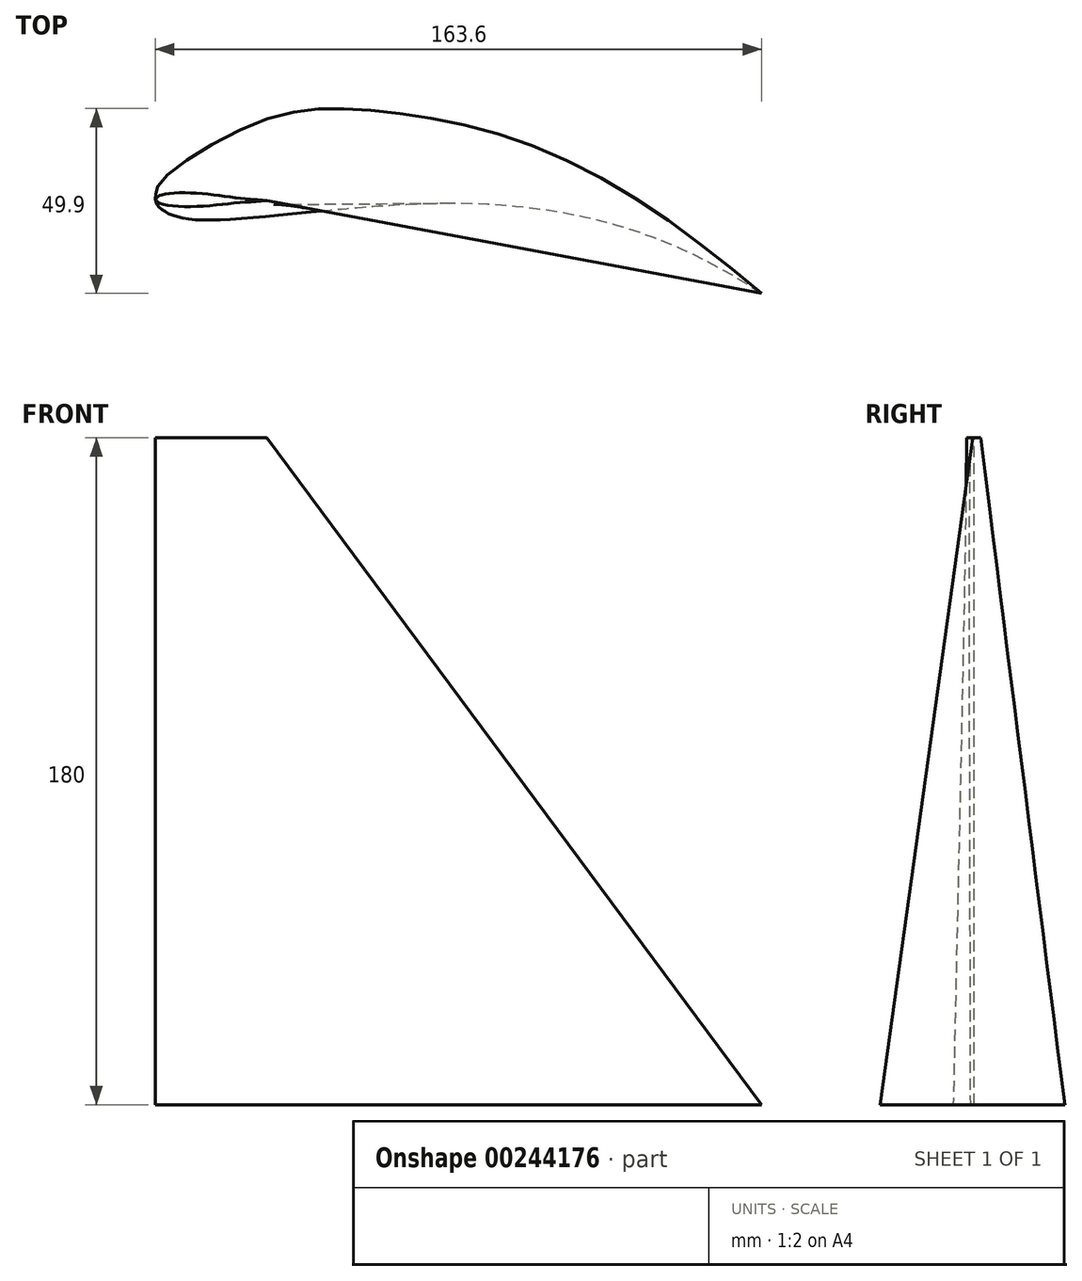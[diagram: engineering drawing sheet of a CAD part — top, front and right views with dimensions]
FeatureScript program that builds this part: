
annotation { "Feature Type Name" : "Feature", "Feature Type Description" : "" }
export const myFeature = defineFeature(function(context is Context, id is Id, definition is map)
    precondition{}
    {
        {
            var Q0;
            Q0=qCreatedBy(makeId("Top.planeOp"),FACE);
            var sketch = newSketch(context, id + "F0", { "sketchPlane" : qUnion([Q0])});
            skLineSegment(sketch, "E0", {"start": v(1.56, 5.68) * mm, "end": v(5.56, 9.57) * mm});
            skLineSegment(sketch, "E1", {"start": v(5.56, 9.57) * mm, "end": v(7.64, 11.4) * mm});
            skLineSegment(sketch, "E2", {"start": v(7.64, 11.4) * mm, "end": v(10.4, 13.54) * mm});
            skLineSegment(sketch, "E3", {"start": v(10.4, 13.54) * mm, "end": v(12.1, 14.65) * mm});
            skLineSegment(sketch, "E4", {"start": v(12.1, 14.65) * mm, "end": v(14.51, 16.01) * mm});
            skLineSegment(sketch, "E5", {"start": v(14.51, 16.01) * mm, "end": v(17.02, 17.22) * mm});
            skLineSegment(sketch, "E6", {"start": v(17.02, 17.22) * mm, "end": v(19.6, 18.28) * mm});
            skLineSegment(sketch, "E7", {"start": v(19.6, 18.28) * mm, "end": v(22.25, 19.22) * mm});
            skLineSegment(sketch, "E8", {"start": v(22.25, 19.22) * mm, "end": v(25.63, 20.25) * mm});
            skLineSegment(sketch, "E9", {"start": v(25.63, 20.25) * mm, "end": v(27.63, 20.8) * mm});
            skLineSegment(sketch, "E10", {"start": v(27.63, 20.8) * mm, "end": v(30.34, 21.45) * mm});
            skLineSegment(sketch, "E11", {"start": v(30.34, 21.45) * mm, "end": v(33.06, 22.02) * mm});
            skLineSegment(sketch, "E12", {"start": v(33.06, 22.02) * mm, "end": v(35.8, 22.52) * mm});
            skLineSegment(sketch, "E13", {"start": v(35.8, 22.52) * mm, "end": v(38.53, 22.94) * mm});
            skLineSegment(sketch, "E14", {"start": v(38.53, 22.94) * mm, "end": v(41.28, 23.3) * mm});
            skLineSegment(sketch, "E15", {"start": v(41.28, 23.3) * mm, "end": v(45.44, 23.69) * mm});
            skLineSegment(sketch, "E16", {"start": v(45.44, 23.69) * mm, "end": v(52.36, 24.01) * mm});
            skLineSegment(sketch, "E17", {"start": v(52.36, 24.01) * mm, "end": v(57.92, 23.98) * mm});
            skLineSegment(sketch, "E18", {"start": v(57.92, 23.98) * mm, "end": v(63.48, 23.67) * mm});
            skLineSegment(sketch, "E19", {"start": v(63.48, 23.67) * mm, "end": v(68.2, 23.2) * mm});
            skLineSegment(sketch, "E20", {"start": v(68.2, 23.2) * mm, "end": v(74.5, 22.25) * mm});
            skLineSegment(sketch, "E21", {"start": v(74.5, 22.25) * mm, "end": v(79.94, 21.16) * mm});
            skLineSegment(sketch, "E22", {"start": v(79.94, 21.16) * mm, "end": v(85.34, 19.84) * mm});
            skLineSegment(sketch, "E23", {"start": v(85.34, 19.84) * mm, "end": v(91.78, 17.96) * mm});
            skLineSegment(sketch, "E24", {"start": v(91.78, 17.96) * mm, "end": v(95.97, 16.57) * mm});
            skLineSegment(sketch, "E25", {"start": v(95.97, 16.57) * mm, "end": v(101.2, 14.66) * mm});
            skLineSegment(sketch, "E26", {"start": v(101.2, 14.66) * mm, "end": v(106.35, 12.57) * mm});
            skLineSegment(sketch, "E27", {"start": v(106.35, 12.57) * mm, "end": v(111.41, 10.3) * mm});
            skLineSegment(sketch, "E28", {"start": v(111.41, 10.3) * mm, "end": v(114.54, 8.79) * mm});
            skLineSegment(sketch, "E29", {"start": v(114.54, 8.79) * mm, "end": v(121.24, 5.25) * mm});
            skLineSegment(sketch, "E30", {"start": v(121.24, 5.25) * mm, "end": v(126.03, 2.48) * mm});
            skLineSegment(sketch, "E31", {"start": v(126.03, 2.48) * mm, "end": v(130.76, -0.45) * mm});
            skLineSegment(sketch, "E32", {"start": v(130.76, -0.45) * mm, "end": v(134.68, -3) * mm});
            skLineSegment(sketch, "E33", {"start": v(134.68, -3) * mm, "end": v(140.13, -6.74) * mm});
            skLineSegment(sketch, "E34", {"start": v(140.13, -6.74) * mm, "end": v(144.69, -10.02) * mm});
            skLineSegment(sketch, "E35", {"start": v(144.69, -10.02) * mm, "end": v(150.73, -14.63) * mm});
            skLineSegment(sketch, "E36", {"start": v(150.73, -14.63) * mm, "end": v(153.15, -16.57) * mm});
            skLineSegment(sketch, "E37", {"start": v(153.15, -16.57) * mm, "end": v(155.17, -18.23) * mm});
            skLineSegment(sketch, "E38", {"start": v(155.17, -18.23) * mm, "end": v(157.28, -19.98) * mm});
            skLineSegment(sketch, "E39", {"start": v(157.28, -19.98) * mm, "end": v(159.53, -21.87) * mm});
            skLineSegment(sketch, "E40", {"start": v(159.53, -21.87) * mm, "end": v(161.04, -23.14) * mm});
            skLineSegment(sketch, "E41", {"start": v(161.04, -23.14) * mm, "end": v(162.55, -24.41) * mm});
            skLineSegment(sketch, "E42", {"start": v(162.55, -24.41) * mm, "end": v(163.03, -24.83) * mm});
            skLineSegment(sketch, "E43", {"start": v(163.03, -24.83) * mm, "end": v(163.34, -25.1) * mm});
            skLineSegment(sketch, "E44", {"start": v(163.34, -25.1) * mm, "end": v(163.57, -25.34) * mm});
            skLineSegment(sketch, "E45", {"start": v(163.57, -25.34) * mm, "end": v(163.6, -25.41) * mm});
            skLineSegment(sketch, "E46", {"start": v(163.6, -25.41) * mm, "end": v(163.5, -25.38) * mm});
            skLineSegment(sketch, "E47", {"start": v(163.5, -25.38) * mm, "end": v(163.25, -25.24) * mm});
            skLineSegment(sketch, "E48", {"start": v(163.25, -25.24) * mm, "end": v(162.89, -25.02) * mm});
            skLineSegment(sketch, "E49", {"start": v(162.89, -25.02) * mm, "end": v(162.42, -24.7) * mm});
            skLineSegment(sketch, "E50", {"start": v(162.42, -24.7) * mm, "end": v(161.85, -24.33) * mm});
            skLineSegment(sketch, "E51", {"start": v(161.85, -24.33) * mm, "end": v(161.2, -23.89) * mm});
            skLineSegment(sketch, "E52", {"start": v(161.2, -23.89) * mm, "end": v(160.46, -23.39) * mm});
            skLineSegment(sketch, "E53", {"start": v(160.46, -23.39) * mm, "end": v(158.82, -22.27) * mm});
            skLineSegment(sketch, "E54", {"start": v(158.82, -22.27) * mm, "end": v(157.02, -21.04) * mm});
            skLineSegment(sketch, "E55", {"start": v(157.02, -21.04) * mm, "end": v(153.51, -18.72) * mm});
            skLineSegment(sketch, "E56", {"start": v(153.51, -18.72) * mm, "end": v(151.5, -17.45) * mm});
            skLineSegment(sketch, "E57", {"start": v(151.5, -17.45) * mm, "end": v(149.82, -16.42) * mm});
            skLineSegment(sketch, "E58", {"start": v(149.82, -16.42) * mm, "end": v(148.21, -15.5) * mm});
            skLineSegment(sketch, "E59", {"start": v(148.21, -15.5) * mm, "end": v(146.7, -14.65) * mm});
            skLineSegment(sketch, "E60", {"start": v(146.7, -14.65) * mm, "end": v(145.24, -13.9) * mm});
            skLineSegment(sketch, "E61", {"start": v(145.24, -13.9) * mm, "end": v(143.85, -13.2) * mm});
            skLineSegment(sketch, "E62", {"start": v(143.85, -13.2) * mm, "end": v(142.52, -12.6) * mm});
            skLineSegment(sketch, "E63", {"start": v(142.52, -12.6) * mm, "end": v(141.24, -12.04) * mm});
            skLineSegment(sketch, "E64", {"start": v(141.24, -12.04) * mm, "end": v(138.82, -11.11) * mm});
            skLineSegment(sketch, "E65", {"start": v(138.82, -11.11) * mm, "end": v(136.53, -10.36) * mm});
            skLineSegment(sketch, "E66", {"start": v(136.53, -10.36) * mm, "end": v(134.32, -9.76) * mm});
            skLineSegment(sketch, "E67", {"start": v(134.32, -9.76) * mm, "end": v(129.95, -8.78) * mm});
            skLineSegment(sketch, "E68", {"start": v(129.95, -8.78) * mm, "end": v(128.13, -8.4) * mm});
            skLineSegment(sketch, "E69", {"start": v(128.13, -8.4) * mm, "end": v(125.32, -7.82) * mm});
            skLineSegment(sketch, "E70", {"start": v(125.32, -7.82) * mm, "end": v(122.86, -7.3) * mm});
            skLineSegment(sketch, "E71", {"start": v(122.86, -7.3) * mm, "end": v(120.3, -6.74) * mm});
            skLineSegment(sketch, "E72", {"start": v(120.3, -6.74) * mm, "end": v(114.98, -5.62) * mm});
            skLineSegment(sketch, "E73", {"start": v(114.98, -5.62) * mm, "end": v(109.42, -4.5) * mm});
            skLineSegment(sketch, "E74", {"start": v(109.42, -4.5) * mm, "end": v(103.71, -3.46) * mm});
            skLineSegment(sketch, "E75", {"start": v(103.71, -3.46) * mm, "end": v(97.93, -2.53) * mm});
            skLineSegment(sketch, "E76", {"start": v(97.93, -2.53) * mm, "end": v(91.13, -1.7) * mm});
            skLineSegment(sketch, "E77", {"start": v(91.13, -1.7) * mm, "end": v(86.47, -1.3) * mm});
            skLineSegment(sketch, "E78", {"start": v(86.47, -1.3) * mm, "end": v(80.86, -1.04) * mm});
            skLineSegment(sketch, "E79", {"start": v(80.86, -1.04) * mm, "end": v(75.32, -0.97) * mm});
            skLineSegment(sketch, "E80", {"start": v(75.32, -0.97) * mm, "end": v(69.81, -1.08) * mm});
            skLineSegment(sketch, "E81", {"start": v(69.81, -1.08) * mm, "end": v(64.32, -1.32) * mm});
            skLineSegment(sketch, "E82", {"start": v(64.32, -1.32) * mm, "end": v(53.96, -2.02) * mm});
            skLineSegment(sketch, "E83", {"start": v(53.96, -2.02) * mm, "end": v(47.7, -2.53) * mm});
            skLineSegment(sketch, "E84", {"start": v(47.7, -2.53) * mm, "end": v(36.53, -3.57) * mm});
            skLineSegment(sketch, "E85", {"start": v(36.53, -3.57) * mm, "end": v(31.03, -4.15) * mm});
            skLineSegment(sketch, "E86", {"start": v(31.03, -4.15) * mm, "end": v(25.3, -4.8) * mm});
            skLineSegment(sketch, "E87", {"start": v(25.3, -4.8) * mm, "end": v(20.36, -5.36) * mm});
            skLineSegment(sketch, "E88", {"start": v(20.36, -5.36) * mm, "end": v(17.7, -5.56) * mm});
            skLineSegment(sketch, "E89", {"start": v(17.7, -5.56) * mm, "end": v(14.96, -5.63) * mm});
            skLineSegment(sketch, "E90", {"start": v(14.96, -5.63) * mm, "end": v(12.13, -5.52) * mm});
            skLineSegment(sketch, "E91", {"start": v(12.13, -5.52) * mm, "end": v(10.66, -5.39) * mm});
            skLineSegment(sketch, "E92", {"start": v(10.66, -5.39) * mm, "end": v(9.15, -5.2) * mm});
            skLineSegment(sketch, "E93", {"start": v(9.15, -5.2) * mm, "end": v(7.78, -4.97) * mm});
            skLineSegment(sketch, "E94", {"start": v(7.78, -4.97) * mm, "end": v(6.02, -4.6) * mm});
            skLineSegment(sketch, "E95", {"start": v(6.02, -4.6) * mm, "end": v(4.48, -4.16) * mm});
            skLineSegment(sketch, "E96", {"start": v(4.48, -4.16) * mm, "end": v(3.06, -3.62) * mm});
            skLineSegment(sketch, "E97", {"start": v(3.06, -3.62) * mm, "end": v(1.82, -2.95) * mm});
            skLineSegment(sketch, "E98", {"start": v(1.82, -2.95) * mm, "end": v(1.3, -2.56) * mm});
            skLineSegment(sketch, "E99", {"start": v(1.3, -2.56) * mm, "end": v(0.85, -2.13) * mm});
            skLineSegment(sketch, "E100", {"start": v(0.85, -2.13) * mm, "end": v(0.5, -1.66) * mm});
            skLineSegment(sketch, "E101", {"start": v(0.5, -1.66) * mm, "end": v(0.25, -1.2) * mm});
            skLineSegment(sketch, "E102", {"start": v(0.25, -1.2) * mm, "end": v(0.07, -0.6) * mm});
            skLineSegment(sketch, "E103", {"start": v(0.07, -0.6) * mm, "end": v(0, 0) * mm});
            skLineSegment(sketch, "E104", {"start": v(0, 0) * mm, "end": v(0.01, 0.63) * mm});
            skLineSegment(sketch, "E105", {"start": v(0.01, 0.63) * mm, "end": v(0.1, 1.3) * mm});
            skLineSegment(sketch, "E106", {"start": v(0.1, 1.3) * mm, "end": v(0.45, 2.7) * mm});
            skLineSegment(sketch, "E107", {"start": v(0.45, 2.7) * mm, "end": v(0.96, 4.17) * mm});
            skLineSegment(sketch, "E108", {"start": v(0.96, 4.17) * mm, "end": v(1.56, 5.68) * mm});
            skSolve(sketch);
        }
        {
            var Q0;
            Q0=qCreatedBy(makeId("Top.planeOp"),FACE);
            var sketch = newSketch(context, id + "F1", { "sketchPlane" : qUnion([Q0])});
            skPoint(sketch, "E109.0", {"position": v(0, 0) * mm});
            skPoint(sketch, "E109.1", {"position": v(0.1, 1.3) * mm});
            skPoint(sketch, "E109.3", {"position": v(27.63, 20.8) * mm});
            skPoint(sketch, "E109.4", {"position": v(57.92, 23.98) * mm});
            skPoint(sketch, "E109.5", {"position": v(106.35, 12.57) * mm});
            skPoint(sketch, "E109.6", {"position": v(0.25, -1.2) * mm});
            skPoint(sketch, "E109.7", {"position": v(3.06, -3.62) * mm});
            skPoint(sketch, "E109.8", {"position": v(14.96, -5.63) * mm});
            skPoint(sketch, "E109.9", {"position": v(80.86, -1.04) * mm});
            skPoint(sketch, "E109.10", {"position": v(163.6, -25.41) * mm});
            skFitSpline(sketch, "E110", {"points": [v(0, 0) * mm, v(0.1, 1.3) * mm, v(0.96, 4.17) * mm, v(27.63, 20.8) * mm, v(57.92, 23.98) * mm, v(106.35, 12.57) * mm, v(163.6, -25.41) * mm], "startDerivative": vector(3.4, 31.63) * mm, "endDerivative": vector(179.4, -153.97) * mm});
            skFitSpline(sketch, "E111", {"points": [v(0, 0) * mm, v(0.25, -1.2) * mm, v(3.06, -3.62) * mm, v(14.96, -5.63) * mm, v(80.86, -1.04) * mm, v(163.6, -25.41) * mm], "startDerivative": vector(0.79, -24.8) * mm, "endDerivative": vector(207.26, -139.02) * mm});
            skSolve(sketch);
        }
        {
            var Q0;
            Q0=qCreatedBy(makeId("Top.planeOp"),FACE);
            cPlane(context, id + "F2", {"entities" : qUnion([Q0]), "cplaneType" : CPlaneType.OFFSET, "offset" : 180 * mm, "width" : 150 * mm, "height" : 150 * mm});
        }
        {
            var Q0;
            Q0=qCreatedBy(id+"F2.planeOp",FACE);
            var sketch = newSketch(context, id + "F3", { "sketchPlane" : qUnion([Q0])});
            skLineSegment(sketch, "E112", {"start": v(0, 0) * mm, "end": v(0.3, 0.38) * mm});
            skLineSegment(sketch, "E113", {"start": v(0.3, 0.38) * mm, "end": v(0.47, 0.56) * mm});
            skLineSegment(sketch, "E114", {"start": v(0.47, 0.56) * mm, "end": v(0.63, 0.72) * mm});
            skLineSegment(sketch, "E115", {"start": v(0.63, 0.72) * mm, "end": v(0.8, 0.86) * mm});
            skLineSegment(sketch, "E116", {"start": v(0.8, 0.86) * mm, "end": v(1, 1) * mm});
            skLineSegment(sketch, "E117", {"start": v(1, 1) * mm, "end": v(1.22, 1.1) * mm});
            skLineSegment(sketch, "E118", {"start": v(1.22, 1.1) * mm, "end": v(1.43, 1.2) * mm});
            skLineSegment(sketch, "E119", {"start": v(1.43, 1.2) * mm, "end": v(1.66, 1.26) * mm});
            skLineSegment(sketch, "E120", {"start": v(1.66, 1.26) * mm, "end": v(1.9, 1.32) * mm});
            skLineSegment(sketch, "E121", {"start": v(1.9, 1.32) * mm, "end": v(2.38, 1.4) * mm});
            skLineSegment(sketch, "E122", {"start": v(2.38, 1.4) * mm, "end": v(3.07, 1.49) * mm});
            skLineSegment(sketch, "E123", {"start": v(3.07, 1.49) * mm, "end": v(4.34, 1.61) * mm});
            skLineSegment(sketch, "E124", {"start": v(4.34, 1.61) * mm, "end": v(5.28, 1.69) * mm});
            skLineSegment(sketch, "E125", {"start": v(5.28, 1.69) * mm, "end": v(6.67, 1.76) * mm});
            skLineSegment(sketch, "E126", {"start": v(6.67, 1.76) * mm, "end": v(7.17, 1.76) * mm});
            skLineSegment(sketch, "E127", {"start": v(7.17, 1.76) * mm, "end": v(8.12, 1.75) * mm});
            skLineSegment(sketch, "E128", {"start": v(8.12, 1.75) * mm, "end": v(9.07, 1.72) * mm});
            skLineSegment(sketch, "E129", {"start": v(9.07, 1.72) * mm, "end": v(10.03, 1.66) * mm});
            skLineSegment(sketch, "E130", {"start": v(10.03, 1.66) * mm, "end": v(11.22, 1.58) * mm});
            skLineSegment(sketch, "E131", {"start": v(11.22, 1.58) * mm, "end": v(12.9, 1.43) * mm});
            skLineSegment(sketch, "E132", {"start": v(12.9, 1.43) * mm, "end": v(14.8, 1.24) * mm});
            skLineSegment(sketch, "E133", {"start": v(14.8, 1.24) * mm, "end": v(16.34, 1.07) * mm});
            skLineSegment(sketch, "E134", {"start": v(16.34, 1.07) * mm, "end": v(18.57, 0.8) * mm});
            skLineSegment(sketch, "E135", {"start": v(18.57, 0.8) * mm, "end": v(20.47, 0.56) * mm});
            skLineSegment(sketch, "E136", {"start": v(20.47, 0.56) * mm, "end": v(21.43, 0.45) * mm});
            skLineSegment(sketch, "E137", {"start": v(21.43, 0.45) * mm, "end": v(22.43, 0.33) * mm});
            skLineSegment(sketch, "E138", {"start": v(22.43, 0.33) * mm, "end": v(23.42, 0.21) * mm});
            skLineSegment(sketch, "E139", {"start": v(23.42, 0.21) * mm, "end": v(24.38, 0.1) * mm});
            skLineSegment(sketch, "E140", {"start": v(24.38, 0.1) * mm, "end": v(24.84, 0.04) * mm});
            skLineSegment(sketch, "E141", {"start": v(24.84, 0.04) * mm, "end": v(25.3, -0.01) * mm});
            skLineSegment(sketch, "E142", {"start": v(25.3, -0.01) * mm, "end": v(25.9, -0.09) * mm});
            skLineSegment(sketch, "E143", {"start": v(25.9, -0.09) * mm, "end": v(26.15, -0.12) * mm});
            skLineSegment(sketch, "E144", {"start": v(26.15, -0.12) * mm, "end": v(26.97, -0.22) * mm});
            skLineSegment(sketch, "E145", {"start": v(26.97, -0.22) * mm, "end": v(27.4, -0.27) * mm});
            skLineSegment(sketch, "E146", {"start": v(27.4, -0.27) * mm, "end": v(27.65, -0.29) * mm});
            skLineSegment(sketch, "E147", {"start": v(27.65, -0.29) * mm, "end": v(27.9, -0.3) * mm});
            skLineSegment(sketch, "E148", {"start": v(27.9, -0.3) * mm, "end": v(28.16, -0.32) * mm});
            skLineSegment(sketch, "E149", {"start": v(28.16, -0.32) * mm, "end": v(28.45, -0.34) * mm});
            skLineSegment(sketch, "E150", {"start": v(28.45, -0.34) * mm, "end": v(28.76, -0.35) * mm});
            skLineSegment(sketch, "E151", {"start": v(28.76, -0.35) * mm, "end": v(28.93, -0.36) * mm});
            skLineSegment(sketch, "E152", {"start": v(28.93, -0.36) * mm, "end": v(29.42, -0.37) * mm});
            skLineSegment(sketch, "E153", {"start": v(29.42, -0.37) * mm, "end": v(29.57, -0.37) * mm});
            skLineSegment(sketch, "E154", {"start": v(29.57, -0.37) * mm, "end": v(29.71, -0.38) * mm});
            skLineSegment(sketch, "E155", {"start": v(29.71, -0.38) * mm, "end": v(29.83, -0.38) * mm});
            skLineSegment(sketch, "E156", {"start": v(29.83, -0.38) * mm, "end": v(29.92, -0.38) * mm});
            skLineSegment(sketch, "E157", {"start": v(29.92, -0.38) * mm, "end": v(29.98, -0.38) * mm});
            skLineSegment(sketch, "E158", {"start": v(29.98, -0.38) * mm, "end": v(30, -0.39) * mm});
            skLineSegment(sketch, "E159", {"start": v(30, -0.39) * mm, "end": v(29.98, -0.39) * mm});
            skLineSegment(sketch, "E160", {"start": v(29.98, -0.39) * mm, "end": v(29.92, -0.4) * mm});
            skLineSegment(sketch, "E161", {"start": v(29.92, -0.4) * mm, "end": v(29.83, -0.4) * mm});
            skLineSegment(sketch, "E162", {"start": v(29.83, -0.4) * mm, "end": v(29.72, -0.4) * mm});
            skLineSegment(sketch, "E163", {"start": v(29.72, -0.4) * mm, "end": v(29.58, -0.4) * mm});
            skLineSegment(sketch, "E164", {"start": v(29.58, -0.4) * mm, "end": v(29.42, -0.4) * mm});
            skLineSegment(sketch, "E165", {"start": v(29.42, -0.4) * mm, "end": v(28.93, -0.42) * mm});
            skLineSegment(sketch, "E166", {"start": v(28.93, -0.42) * mm, "end": v(28.76, -0.42) * mm});
            skLineSegment(sketch, "E167", {"start": v(28.76, -0.42) * mm, "end": v(28.45, -0.43) * mm});
            skLineSegment(sketch, "E168", {"start": v(28.45, -0.43) * mm, "end": v(28.17, -0.44) * mm});
            skLineSegment(sketch, "E169", {"start": v(28.17, -0.44) * mm, "end": v(27.9, -0.46) * mm});
            skLineSegment(sketch, "E170", {"start": v(27.9, -0.46) * mm, "end": v(27.65, -0.47) * mm});
            skLineSegment(sketch, "E171", {"start": v(27.65, -0.47) * mm, "end": v(27.4, -0.49) * mm});
            skLineSegment(sketch, "E172", {"start": v(27.4, -0.49) * mm, "end": v(26.96, -0.52) * mm});
            skLineSegment(sketch, "E173", {"start": v(26.96, -0.52) * mm, "end": v(26.14, -0.6) * mm});
            skLineSegment(sketch, "E174", {"start": v(26.14, -0.6) * mm, "end": v(25.86, -0.62) * mm});
            skLineSegment(sketch, "E175", {"start": v(25.86, -0.62) * mm, "end": v(25.3, -0.68) * mm});
            skLineSegment(sketch, "E176", {"start": v(25.3, -0.68) * mm, "end": v(24.84, -0.72) * mm});
            skLineSegment(sketch, "E177", {"start": v(24.84, -0.72) * mm, "end": v(24.37, -0.77) * mm});
            skLineSegment(sketch, "E178", {"start": v(24.37, -0.77) * mm, "end": v(23.4, -0.86) * mm});
            skLineSegment(sketch, "E179", {"start": v(23.4, -0.86) * mm, "end": v(22.42, -0.95) * mm});
            skLineSegment(sketch, "E180", {"start": v(22.42, -0.95) * mm, "end": v(21.43, -1.04) * mm});
            skLineSegment(sketch, "E181", {"start": v(21.43, -1.04) * mm, "end": v(20.45, -1.13) * mm});
            skLineSegment(sketch, "E182", {"start": v(20.45, -1.13) * mm, "end": v(18.55, -1.3) * mm});
            skLineSegment(sketch, "E183", {"start": v(18.55, -1.3) * mm, "end": v(16.28, -1.52) * mm});
            skLineSegment(sketch, "E184", {"start": v(16.28, -1.52) * mm, "end": v(12.87, -1.8) * mm});
            skLineSegment(sketch, "E185", {"start": v(12.87, -1.8) * mm, "end": v(11.19, -1.9) * mm});
            skLineSegment(sketch, "E186", {"start": v(11.19, -1.9) * mm, "end": v(10, -1.95) * mm});
            skLineSegment(sketch, "E187", {"start": v(10, -1.95) * mm, "end": v(9.03, -1.98) * mm});
            skLineSegment(sketch, "E188", {"start": v(9.03, -1.98) * mm, "end": v(8.08, -1.98) * mm});
            skLineSegment(sketch, "E189", {"start": v(8.08, -1.98) * mm, "end": v(7.13, -1.96) * mm});
            skLineSegment(sketch, "E190", {"start": v(7.13, -1.96) * mm, "end": v(6.6, -1.93) * mm});
            skLineSegment(sketch, "E191", {"start": v(6.6, -1.93) * mm, "end": v(5.24, -1.83) * mm});
            skLineSegment(sketch, "E192", {"start": v(5.24, -1.83) * mm, "end": v(4.3, -1.74) * mm});
            skLineSegment(sketch, "E193", {"start": v(4.3, -1.74) * mm, "end": v(3.04, -1.58) * mm});
            skLineSegment(sketch, "E194", {"start": v(3.04, -1.58) * mm, "end": v(2.35, -1.47) * mm});
            skLineSegment(sketch, "E195", {"start": v(2.35, -1.47) * mm, "end": v(1.87, -1.37) * mm});
            skLineSegment(sketch, "E196", {"start": v(1.87, -1.37) * mm, "end": v(1.64, -1.3) * mm});
            skLineSegment(sketch, "E197", {"start": v(1.64, -1.3) * mm, "end": v(1.41, -1.22) * mm});
            skLineSegment(sketch, "E198", {"start": v(1.41, -1.22) * mm, "end": v(1.2, -1.13) * mm});
            skLineSegment(sketch, "E199", {"start": v(1.2, -1.13) * mm, "end": v(1, -1.01) * mm});
            skLineSegment(sketch, "E200", {"start": v(1, -1.01) * mm, "end": v(0.77, -0.86) * mm});
            skLineSegment(sketch, "E201", {"start": v(0.77, -0.86) * mm, "end": v(0.62, -0.73) * mm});
            skLineSegment(sketch, "E202", {"start": v(0.62, -0.73) * mm, "end": v(0.46, -0.57) * mm});
            skLineSegment(sketch, "E203", {"start": v(0.46, -0.57) * mm, "end": v(0.3, -0.38) * mm});
            skLineSegment(sketch, "E204", {"start": v(0.3, -0.38) * mm, "end": v(0, 0) * mm});
            skSolve(sketch);
        }
        {
            var Q0;
            Q0=qCreatedBy(id+"F2.planeOp",FACE);
            var sketch = newSketch(context, id + "F4", { "sketchPlane" : qUnion([Q0])});
            skPoint(sketch, "E205.0", {"position": v(0, 0) * mm});
            skPoint(sketch, "E205.1", {"position": v(0.47, 0.56) * mm});
            skPoint(sketch, "E205.2", {"position": v(1, 1) * mm});
            skPoint(sketch, "E205.3", {"position": v(8.12, 1.75) * mm});
            skPoint(sketch, "E205.4", {"position": v(20.47, 0.56) * mm});
            skPoint(sketch, "E205.5", {"position": v(30, -0.39) * mm});
            skPoint(sketch, "E205.6", {"position": v(20.45, -1.13) * mm});
            skPoint(sketch, "E205.7", {"position": v(8.08, -1.98) * mm});
            skPoint(sketch, "E205.8", {"position": v(0.46, -0.57) * mm});
            skPoint(sketch, "E205.9", {"position": v(1, -1.01) * mm});
            skFitSpline(sketch, "E206", {"points": [v(0, 0) * mm, v(0.47, 0.56) * mm, v(1, 1) * mm, v(8.12, 1.75) * mm, v(20.47, 0.56) * mm, v(30, -0.39) * mm], "startDerivative": vector(6.36, 7.54) * mm, "endDerivative": vector(32.55, -2.82) * mm});
            skFitSpline(sketch, "E207", {"points": [v(0, 0) * mm, v(0.46, -0.57) * mm, v(1, -1.01) * mm, v(8.08, -1.98) * mm, v(20.45, -1.13) * mm, v(30, -0.39) * mm], "startDerivative": vector(6.25, -7.63) * mm, "endDerivative": vector(32.6, 2.17) * mm});
            skSolve(sketch);
        }
        {
            var Q0;
            Q0=makeQuery(id+"F1.imprint","IMPRINT",FACE,{"disambiguationData":[TD([[makeQuery(id+"F1.imprint","IMPRINT",EDGE,{"derivedFrom":sQuery(id+"F1.wireOp",EDGE,"E110")}),-1.0]])]});
            var Q1;
            Q1=makeQuery(id+"F4.imprint","IMPRINT",FACE,{"disambiguationData":[TD([[makeQuery(id+"F4.imprint","IMPRINT",EDGE,{"derivedFrom":sQuery(id+"F4.wireOp",EDGE,"E206")}),-1.0]])]});
            loft(context, id + "F5", {"sheetProfilesArray" : [{ "sheetProfileEntities" : qUnion([Q0]) }, { "sheetProfileEntities" : qUnion([Q1]) }]});
        }
    });
